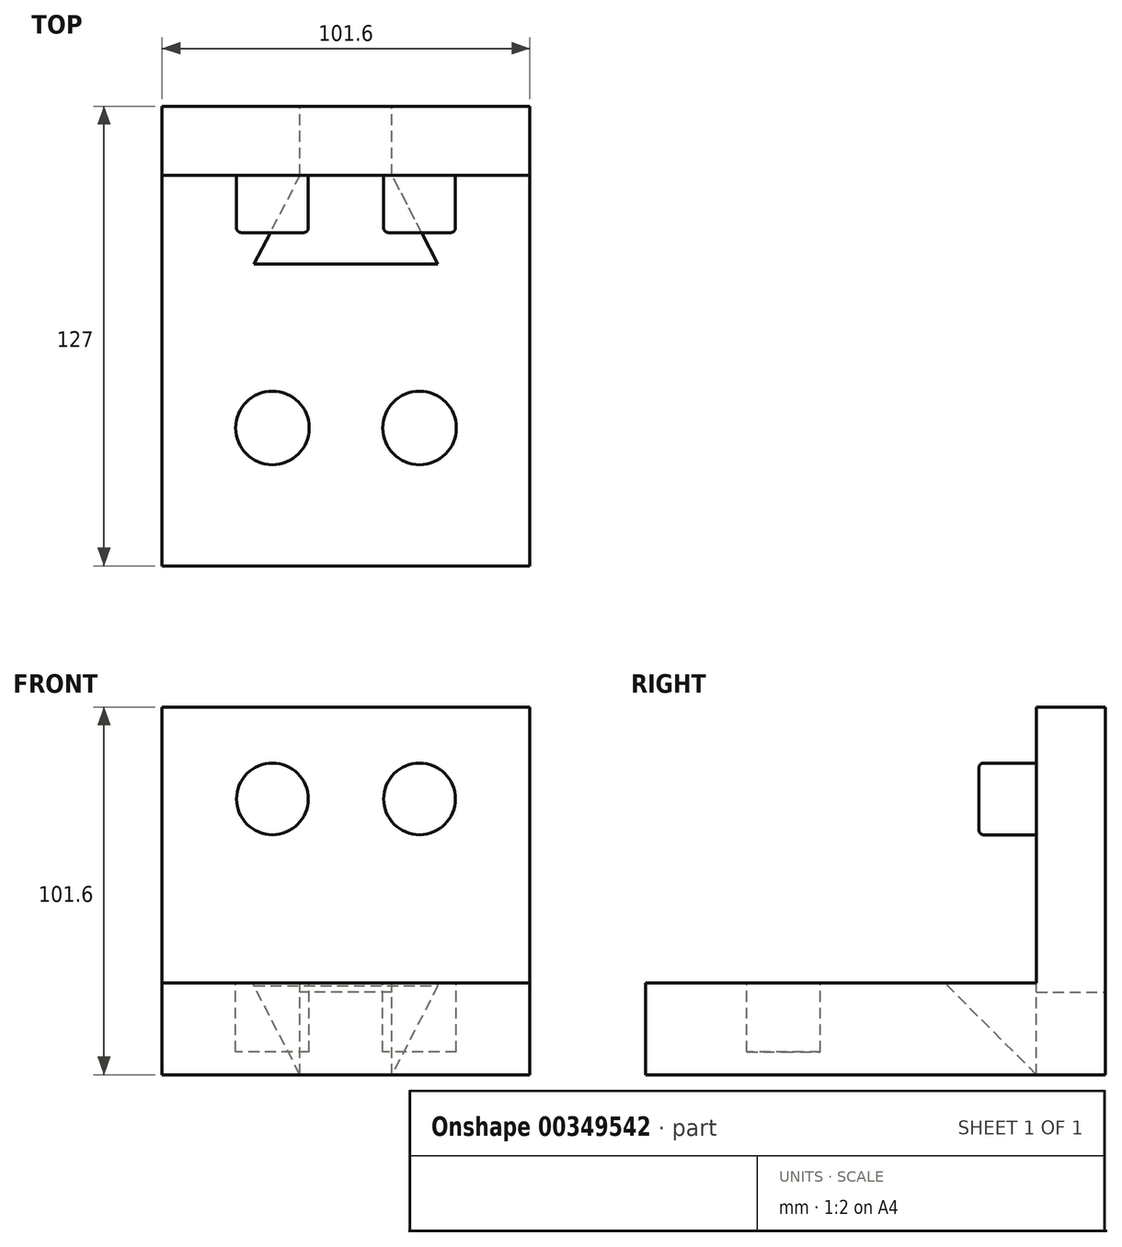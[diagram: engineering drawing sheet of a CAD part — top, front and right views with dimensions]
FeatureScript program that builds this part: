
annotation { "Feature Type Name" : "Feature", "Feature Type Description" : "" }
export const myFeature = defineFeature(function(context is Context, id is Id, definition is map)
    precondition{}
    {
        {
            var Q0;
            Q0=qCreatedBy(makeId("Top.planeOp"),FACE);
            var sketch = newSketch(context, id + "F0", { "sketchPlane" : qUnion([Q0])});
            skLineSegment(sketch, "E0", {"start": v(0, 0) * mm, "end": v(0, 127) * mm});
            skLineSegment(sketch, "E1", {"start": v(0, 127) * mm, "end": v(101.6, 127) * mm});
            skLineSegment(sketch, "E2", {"start": v(101.6, 127) * mm, "end": v(101.6, 0) * mm});
            skLineSegment(sketch, "E3", {"start": v(101.6, 0) * mm, "end": v(0, 0) * mm});
            skSolve(sketch);
        }
        {
            var Q0;
            Q0 = qSketchRegion(id + "F0", true);
            extrude(context, id + "F1", {"entities" : qUnion([Q0]), "depth" : 25.4 * mm});
        }
        {
            var Q0;
            Q0=makeQuery(id+"F1.opExtrude","CAP_FACE",FACE,{"disambiguationData":[OSD([sQuery(id+"F0.wireOp",EDGE,"E0"),sQuery(id+"F0.wireOp",EDGE,"E1"),sQuery(id+"F0.wireOp",EDGE,"E2"),sQuery(id+"F0.wireOp",EDGE,"E3")])],"isStart":false});
            var sketch = newSketch(context, id + "F2", { "sketchPlane" : qUnion([Q0])});
            skCircle(sketch, "E4", {"center": v(30.48, 38.1) * mm, "radius": 10.16 * mm});
            skCircle(sketch, "E5", {"center": v(71.12, 38.1) * mm, "radius": 10.16 * mm});
            skSolve(sketch);
        }
        {
            var Q0;
            Q0 = qSketchRegion(id + "F2", true);
            extrude(context, id + "F3", {"entities" : qUnion([Q0]), "operationType" : NewBodyOperationType.REMOVE, "oppositeDirection" : true, "depth" : 19.05 * mm});
        }
        {
            var Q0;
            Q0=makeQuery(id+"F1.opExtrude","SWEPT_FACE",FACE,{"disambiguationData":[OSD([sQuery(id+"F0.wireOp",EDGE,"E2")])]});
            var sketch = newSketch(context, id + "F4", { "sketchPlane" : qUnion([Q0])});
            skLineSegment(sketch, "E6", {"start": v(127, 25.4) * mm, "end": v(127, 101.6) * mm});
            skLineSegment(sketch, "E7", {"start": v(127, 101.6) * mm, "end": v(107.95, 101.6) * mm});
            skLineSegment(sketch, "E8", {"start": v(107.95, 101.6) * mm, "end": v(107.95, 25.4) * mm});
            skLineSegment(sketch, "E9", {"start": v(107.95, 25.4) * mm, "end": v(127, 25.4) * mm});
            skSolve(sketch);
        }
        {
            var Q0;
            Q0 = qSketchRegion(id + "F4", true);
            extrude(context, id + "F5", {"entities" : qUnion([Q0]), "operationType" : NewBodyOperationType.ADD, "oppositeDirection" : true, "depth" : 101.6 * mm});
        }
        {
            var Q0;
            Q0=makeQuery(id+"F5.opExtrude","SWEPT_FACE",FACE,{"disambiguationData":[OSD([sQuery(id+"F4.wireOp",EDGE,"E8")])]});
            var sketch = newSketch(context, id + "F6", { "sketchPlane" : qUnion([Q0])});
            skCircle(sketch, "E10", {"center": v(30.48, 76.2) * mm, "radius": 9.9 * mm});
            skPoint(sketch, "E11.endSnap0", {"position": v(50.8, 101.6) * mm});
            skCircle(sketch, "E12.MirrorC", {"center": v(71.12, 76.2) * mm, "radius": 9.9 * mm});
            skSolve(sketch);
        }
        {
            var Q0;
            Q0 = qSketchRegion(id + "F6", true);
            extrude(context, id + "F7", {"entities" : qUnion([Q0]), "operationType" : NewBodyOperationType.ADD, "depth" : 15.88 * mm});
        }
        {
            var Q0;
            Q0=makeQuery(id+"F7.opExtrude","CAP_EDGE",EDGE,{"disambiguationData":[OSD([sQuery(id+"F6.wireOp",EDGE,"E12.MirrorC")])],"isStart":false});
            var Q1;
            Q1=makeQuery(id+"F7.opExtrude","CAP_EDGE",EDGE,{"disambiguationData":[OSD([sQuery(id+"F6.wireOp",EDGE,"E10")])],"isStart":false});
            fillet(context, id + "F8", {"entities" : qUnion([Q0, Q1]), "radius" : 1.27 * mm, "tangentPropagation" : true, "allowEdgeOverflow" : false});
        }
        {
            var Q0;
            Q0=makeQuery(id+"F1.opExtrude","CAP_FACE",FACE,{"disambiguationData":[OSD([sQuery(id+"F0.wireOp",EDGE,"E0"),sQuery(id+"F0.wireOp",EDGE,"E1"),sQuery(id+"F0.wireOp",EDGE,"E2"),sQuery(id+"F0.wireOp",EDGE,"E3")])],"isStart":false});
            var sketch = newSketch(context, id + "F9", { "sketchPlane" : qUnion([Q0])});
            skLineSegment(sketch, "E13", {"start": v(38.1, 107.95) * mm, "end": v(25.4, 83.38) * mm});
            skLineSegment(sketch, "E14", {"start": v(25.4, 83.38) * mm, "end": v(76.2, 83.38) * mm});
            skLineSegment(sketch, "E15", {"start": v(76.2, 83.38) * mm, "end": v(63.5, 107.95) * mm});
            skLineSegment(sketch, "E16", {"start": v(63.5, 107.95) * mm, "end": v(38.1, 107.95) * mm});
            skSolve(sketch);
        }
        {
            var Q0;
            Q0 = qSketchRegion(id + "F9", true);
            extrude(context, id + "F10", {"entities" : qUnion([Q0]), "operationType" : NewBodyOperationType.REMOVE, "endBound" : BoundingType.THROUGH_ALL, "oppositeDirection" : true, "depth" : 25.4 * mm});
        }
        {
            var Q0;
            Q0=makeQuery(id+"F5.boolean.opBoolean","MERGE",FACE,{"derivedFrom":[makeQuery(id+"F1.opExtrude","SWEPT_FACE",FACE,{"disambiguationData":[OSD([sQuery(id+"F0.wireOp",EDGE,"E1")])]}),makeQuery(id+"F5.opExtrude","SWEPT_FACE",FACE,{"disambiguationData":[OSD([sQuery(id+"F4.wireOp",EDGE,"E6")])]})]});
            var sketch = newSketch(context, id + "F11", { "sketchPlane" : qUnion([Q0])});
            skLineSegment(sketch, "E17", {"start": v(-63.5, 0) * mm, "end": v(-63.5, 22.86) * mm});
            skLineSegment(sketch, "E18", {"start": v(-63.5, 22.86) * mm, "end": v(-38.1, 22.86) * mm});
            skLineSegment(sketch, "E19", {"start": v(-38.1, 22.86) * mm, "end": v(-38.1, 0) * mm});
            skLineSegment(sketch, "E20", {"start": v(-63.5, 0) * mm, "end": v(-38.1, 0) * mm});
            skSolve(sketch);
        }
        {
            var Q0;
            Q0 = qSketchRegion(id + "F11", true);
            extrude(context, id + "F12", {"entities" : qUnion([Q0]), "operationType" : NewBodyOperationType.REMOVE, "oppositeDirection" : true, "depth" : 25.4 * mm});
        }
        {
            var Q0;
            Q0=makeQuery(id+"F5.boolean.opBoolean","MERGE",FACE,{"derivedFrom":[makeQuery(id+"F1.opExtrude","SWEPT_FACE",FACE,{"disambiguationData":[OSD([sQuery(id+"F0.wireOp",EDGE,"E2")])]}),makeQuery(id+"F5.opExtrude","CAP_FACE",FACE,{"disambiguationData":[OSD([sQuery(id+"F4.wireOp",EDGE,"E6"),sQuery(id+"F4.wireOp",EDGE,"E7"),sQuery(id+"F4.wireOp",EDGE,"E8"),sQuery(id+"F4.wireOp",EDGE,"E9")])],"isStart":true})]});
            var sketch = newSketch(context, id + "F13", { "sketchPlane" : qUnion([Q0])});
            skLineSegment(sketch, "E21", {"start": v(107.95, 0) * mm, "end": v(82.55, 0) * mm});
            skLineSegment(sketch, "E22", {"start": v(82.55, 0) * mm, "end": v(82.55, 25.4) * mm});
            skLineSegment(sketch, "E23", {"start": v(82.55, 25.4) * mm, "end": v(107.95, 0) * mm});
            skSolve(sketch);
        }
        {
            var Q0;
            Q0 = qSketchRegion(id + "F13", true);
            extrude(context, id + "F14", {"entities" : qUnion([Q0]), "operationType" : NewBodyOperationType.ADD, "oppositeDirection" : true, "depth" : 101.6 * mm});
        }
    });
